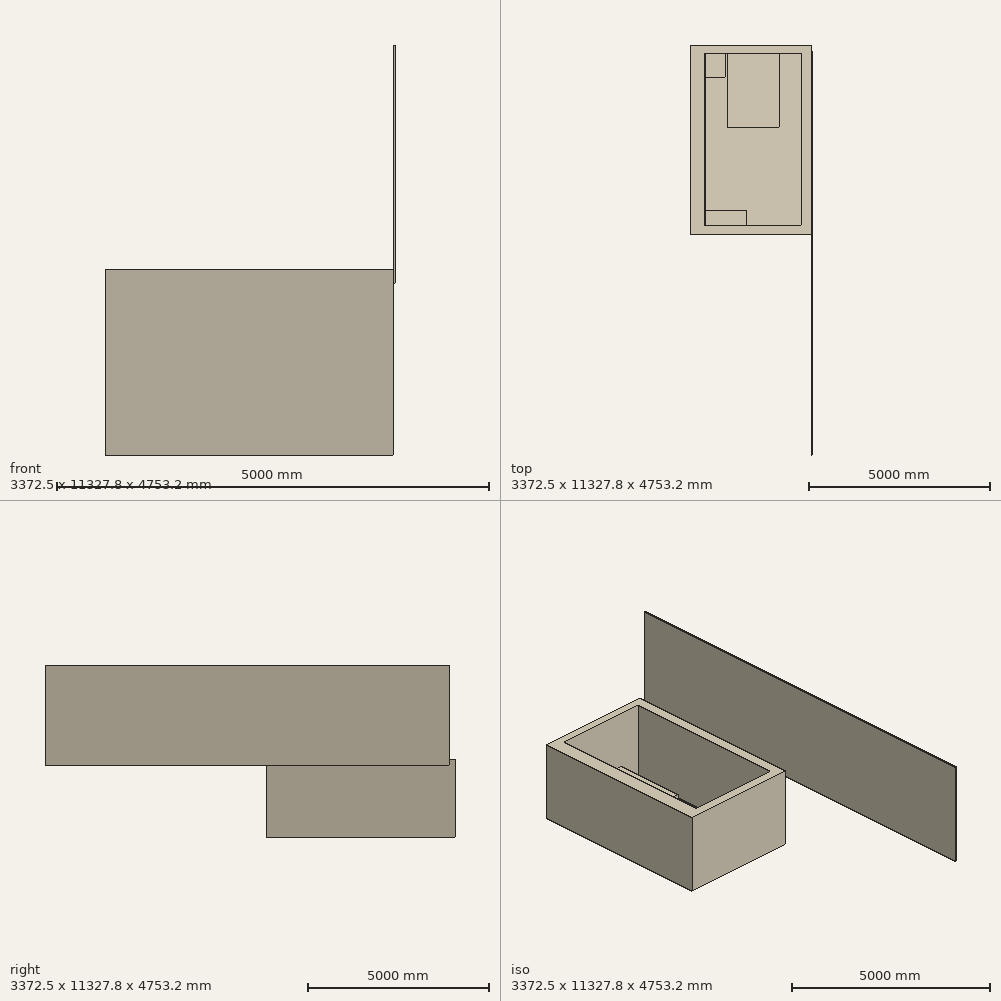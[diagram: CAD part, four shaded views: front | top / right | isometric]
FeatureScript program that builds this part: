
annotation { "Feature Type Name" : "Feature", "Feature Type Description" : "" }
export const myFeature = defineFeature(function(context is Context, id is Id, definition is map)
    precondition{}
    {
        {
            var Q0;
            Q0=qCreatedBy(makeId("Top.planeOp"),FACE);
            var sketch = newSketch(context, id + "F0", { "sketchPlane" : qUnion([Q0])});
            skLineSegment(sketch, "E0.top", {"start": v(-1104.9, -1259.39) * mm, "end": v(1562.1, -1259.39) * mm});
            skLineSegment(sketch, "E0.left", {"start": v(-1104.9, 3490.41) * mm, "end": v(-1104.9, -1259.39) * mm});
            skLineSegment(sketch, "E0.right", {"start": v(1562.1, 3490.41) * mm, "end": v(1562.1, -1259.39) * mm});
            skLineSegment(sketch, "E1", {"start": v(-1104.9, 3490.41) * mm, "end": v(1562.1, 3490.41) * mm});
            skLineSegment(sketch, "E2", {"start": v(-1503.24, 3706.06) * mm, "end": v(1843.83, 3706.06) * mm});
            skLineSegment(sketch, "E3", {"start": v(1843.83, 3706.06) * mm, "end": v(1843.83, -1513.43) * mm});
            skLineSegment(sketch, "E4", {"start": v(1843.83, -1513.43) * mm, "end": v(-1503.24, -1513.43) * mm});
            skLineSegment(sketch, "E5", {"start": v(-1503.24, -1513.43) * mm, "end": v(-1503.24, 3706.06) * mm});
            skSolve(sketch);
        }
        {
            var Q0;
            Q0=makeQuery(id+"F0.imprint","IMPRINT",FACE,{"disambiguationData":[TD([[makeQuery(id+"F0.imprint","IMPRINT",EDGE,{"derivedFrom":sQuery(id+"F0.wireOp",EDGE,"E0.top")}),-1.0]])]});
            extrude(context, id + "F1", {"entities" : qUnion([Q0]), "depth" : 2133.6 * mm});
        }
        {
            var Q0;
            Q0=qCreatedBy(makeId("Top.planeOp"),FACE);
            var sketch = newSketch(context, id + "F2", { "sketchPlane" : qUnion([Q0])});
            skLineSegment(sketch, "E6.bottom", {"start": v(-1086.5, 3490.41) * mm, "end": v(1558.96, 3490.41) * mm});
            skLineSegment(sketch, "E6.top", {"start": v(-1086.5, -1264.82) * mm, "end": v(1558.96, -1264.82) * mm});
            skLineSegment(sketch, "E6.left", {"start": v(-1086.5, 3490.41) * mm, "end": v(-1086.5, -1264.82) * mm});
            skLineSegment(sketch, "E6.right", {"start": v(1558.96, 3490.41) * mm, "end": v(1558.96, -1264.82) * mm});
            skSolve(sketch);
        }
        {
            var Q0;
            Q0=makeQuery(id+"F2.imprint","IMPRINT",FACE,{"disambiguationData":[TD([[makeQuery(id+"F2.imprint","IMPRINT",EDGE,{"derivedFrom":sQuery(id+"F2.wireOp",EDGE,"E6.bottom")}),-1.0]])]});
            extrude(context, id + "F3", {"entities" : qUnion([Q0]), "operationType" : NewBodyOperationType.REMOVE, "oppositeDirection" : true, "depth" : 25.4 * mm});
        }
        {
            var Q0;
            Q0=makeQuery(id+"F1.opExtrude","CAP_FACE",FACE,{"disambiguationData":[OSD([sQuery(id+"F0.wireOp",EDGE,"E0.top"),sQuery(id+"F0.wireOp",EDGE,"E0.left"),sQuery(id+"F0.wireOp",EDGE,"E0.right"),sQuery(id+"F0.wireOp",EDGE,"E1"),sQuery(id+"F0.wireOp",EDGE,"E2"),sQuery(id+"F0.wireOp",EDGE,"E3"),sQuery(id+"F0.wireOp",EDGE,"E4"),sQuery(id+"F0.wireOp",EDGE,"E5")])],"isStart":false});
            extrude(context, id + "F4", {"entities" : qUnion([Q0]), "operationType" : NewBodyOperationType.ADD, "depth" : 25.4 * mm});
        }
        {
            var Q0;
            Q0=qCreatedBy(makeId("Top.planeOp"),FACE);
            var sketch = newSketch(context, id + "F5", { "sketchPlane" : qUnion([Q0])});
            skLineSegment(sketch, "E7", {"start": v(-1086.5, 3482.17) * mm, "end": v(1567.2, 3482.17) * mm});
            skLineSegment(sketch, "E8", {"start": v(1567.2, 3482.17) * mm, "end": v(1567.2, -1264.82) * mm});
            skLineSegment(sketch, "E9", {"start": v(1567.2, -1264.82) * mm, "end": v(-1078.26, -1264.82) * mm});
            skLineSegment(sketch, "E10", {"start": v(-1078.26, -1264.82) * mm, "end": v(-1086.5, 3482.17) * mm});
            skSolve(sketch);
        }
        {
            var Q0;
            Q0=makeQuery(id+"F5.imprint","IMPRINT",FACE,{"disambiguationData":[TD([[makeQuery(id+"F5.imprint","IMPRINT",EDGE,{"derivedFrom":sQuery(id+"F5.wireOp",EDGE,"E7")}),-1.0]])]});
            extrude(context, id + "F6", {"entities" : qUnion([Q0]), "operationType" : NewBodyOperationType.ADD, "depth" : 25.4 * mm});
        }
        {
            var Q0;
            Q0=makeQuery(id+"F6.opExtrude","CAP_FACE",FACE,{"disambiguationData":[OSD([sQuery(id+"F5.wireOp",EDGE,"E7"),sQuery(id+"F5.wireOp",EDGE,"E8"),sQuery(id+"F5.wireOp",EDGE,"E9"),sQuery(id+"F5.wireOp",EDGE,"E10")])],"isStart":false});
            var sketch = newSketch(context, id + "F7", { "sketchPlane" : qUnion([Q0])});
            skLineSegment(sketch, "E11.bottom", {"start": v(-492.45, 3482.17) * mm, "end": v(968.05, 3482.17) * mm});
            skLineSegment(sketch, "E11.top", {"start": v(-492.45, 1450.17) * mm, "end": v(968.05, 1450.17) * mm});
            skLineSegment(sketch, "E11.left", {"start": v(-492.45, 3482.17) * mm, "end": v(-492.45, 1450.17) * mm});
            skLineSegment(sketch, "E11.right", {"start": v(968.05, 3482.17) * mm, "end": v(968.05, 1450.17) * mm});
            skSolve(sketch);
        }
        {
            var Q0;
            Q0=makeQuery(id+"F7.imprint","IMPRINT",FACE,{"disambiguationData":[TD([[makeQuery(id+"F7.imprint","IMPRINT",EDGE,{"derivedFrom":sQuery(id+"F7.wireOp",EDGE,"E11.bottom")}),-1.0]])]});
            extrude(context, id + "F8", {"entities" : qUnion([Q0]), "operationType" : NewBodyOperationType.ADD, "depth" : 584.2 * mm});
        }
        {
            var Q0;
            Q0=makeQuery(id+"F6.opExtrude","CAP_FACE",FACE,{"disambiguationData":[OSD([sQuery(id+"F5.wireOp",EDGE,"E7"),sQuery(id+"F5.wireOp",EDGE,"E8"),sQuery(id+"F5.wireOp",EDGE,"E9"),sQuery(id+"F5.wireOp",EDGE,"E10")])],"isStart":false});
            var sketch = newSketch(context, id + "F9", { "sketchPlane" : qUnion([Q0])});
            skLineSegment(sketch, "E12.bottom", {"start": v(-1086.5, 3482.17) * mm, "end": v(-546.75, 3482.17) * mm});
            skLineSegment(sketch, "E12.top", {"start": v(-1086.5, 2821.77) * mm, "end": v(-546.75, 2821.77) * mm});
            skLineSegment(sketch, "E12.left", {"start": v(-1086.5, 3482.17) * mm, "end": v(-1086.5, 2821.77) * mm});
            skLineSegment(sketch, "E12.right", {"start": v(-546.75, 3482.17) * mm, "end": v(-546.75, 2821.77) * mm});
            skSolve(sketch);
        }
        {
            var Q0;
            {var subQ0=sQuery(id+"F9.wireOp",EDGE,"E12.bottom");Q0=makeQuery(id+"F9.imprint","IMPRINT",FACE,{"disambiguationData":[TD([[makeQuery(id+"F9.imprint","IMPRINT",EDGE,{"derivedFrom":subQ0}),-1.0]])]});}
            extrude(context, id + "F10", {"entities" : qUnion([Q0]), "operationType" : NewBodyOperationType.ADD, "depth" : 584.2 * mm});
        }
        {
            var Q0;
            Q0=makeQuery(id+"F6.opExtrude","CAP_FACE",FACE,{"disambiguationData":[OSD([sQuery(id+"F5.wireOp",EDGE,"E7"),sQuery(id+"F5.wireOp",EDGE,"E8"),sQuery(id+"F5.wireOp",EDGE,"E9"),sQuery(id+"F5.wireOp",EDGE,"E10")])],"isStart":false});
            var sketch = newSketch(context, id + "F11", { "sketchPlane" : qUnion([Q0])});
            skLineSegment(sketch, "E13.bottom", {"start": v(-1078.27, -1259.39) * mm, "end": v(39.33, -1259.39) * mm});
            skLineSegment(sketch, "E13.top", {"start": v(-1078.27, -852.99) * mm, "end": v(39.33, -852.99) * mm});
            skLineSegment(sketch, "E13.left", {"start": v(-1078.27, -1259.39) * mm, "end": v(-1078.27, -852.99) * mm});
            skLineSegment(sketch, "E13.right", {"start": v(39.33, -1259.39) * mm, "end": v(39.33, -852.99) * mm});
            skSolve(sketch);
        }
        {
            var Q0;
            Q0=makeQuery(id+"F11.imprint","IMPRINT",FACE,{"disambiguationData":[TD([[makeQuery(id+"F11.imprint","IMPRINT",EDGE,{"derivedFrom":sQuery(id+"F11.wireOp",EDGE,"E13.bottom")}),1.0]])]});
            extrude(context, id + "F12", {"entities" : qUnion([Q0]), "operationType" : NewBodyOperationType.ADD, "depth" : 1473.2 * mm});
        }
        {
            var Q0;
            {var subQ0=sQuery(id+"F0.wireOp",EDGE,"E3");Q0=makeQuery(id+"F4.boolean.opBoolean","MERGE",FACE,{"derivedFrom":[makeQuery(id+"F1.opExtrude","SWEPT_FACE",FACE,{"disambiguationData":[OSD([subQ0])]}),makeQuery(id+"F4.opExtrude","SWEPT_FACE",FACE,{"disambiguationData":[OSD([subQ0])]})]});}
            var sketch = newSketch(context, id + "F14", { "sketchPlane" : qUnion([Q0])});
            skLineSegment(sketch, "E14.bottom", {"start": v(-7621.72, 1991.72) * mm, "end": v(3534.64, 1991.72) * mm});
            skLineSegment(sketch, "E14.top", {"start": v(-7621.72, 4753.25) * mm, "end": v(3534.64, 4753.25) * mm});
            skLineSegment(sketch, "E14.left", {"start": v(-7621.72, 1991.72) * mm, "end": v(-7621.72, 4753.25) * mm});
            skLineSegment(sketch, "E14.right", {"start": v(3534.64, 1991.72) * mm, "end": v(3534.64, 4753.25) * mm});
            skSolve(sketch);
        }
        {
            var Q0;
            Q0 = qSketchRegion(id + "F14", true);
            extrude(context, id + "F13", {"entities" : qUnion([Q0]), "operationType" : NewBodyOperationType.ADD, "depth" : 25.4 * mm});
        }
    });
